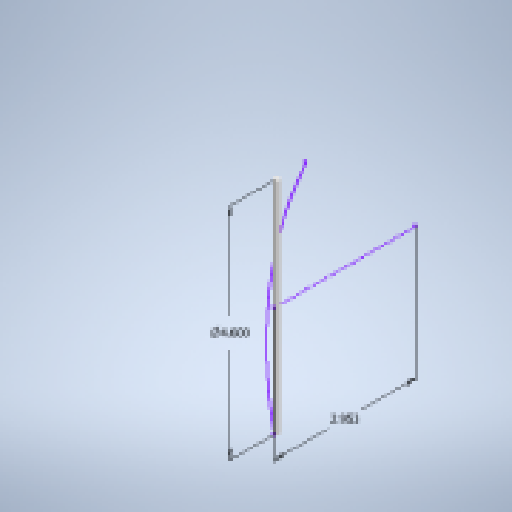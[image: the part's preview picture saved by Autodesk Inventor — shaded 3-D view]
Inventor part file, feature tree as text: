
AUTODESK INVENTOR PART (.ipt)
format: ipt  version: 2023.2 (Build 272271000, 271)  size: 147,968 bytes
history: native  units: in
note: dims shown in document units (in); Inventor stores cm internally (conversion verified against a paired STEP export)
features: sketch x2, other x2, extrude x1, pattern_linear x1
ambient origin geometry x8: Origin, YZ Plane, XZ Plane, XY Plane, X Axis, Y Axis, Z Axis, Center Point
bodies: Solid1 (feature_tree)
feature tree (6):
  sketch  "Sketch3"  dims[d0=0.1181in d1=4.6in d2=0.0in d3=2.9528in d4=0.0984in d5=4.6in d6=0.0in d7=1.5748in d9=0.3937in d11=1.0in d12=1.3in]
  other  "Work Point1"
  extrude  "Extrusion1"  Depth=4.6in TaperAngle=0.0deg
  pattern_linear  "Rectangular Pattern1"  Spacing1=2.9528in  [1 undecoded]
  sketch  "3D Sketch1"
  other  "Helical Curve1"
note: 1 required parameter value undecoded (feature->parameter linkage not recoverable at this tier; creation-order binding heuristic only, values carry confidence <= 0.55)
